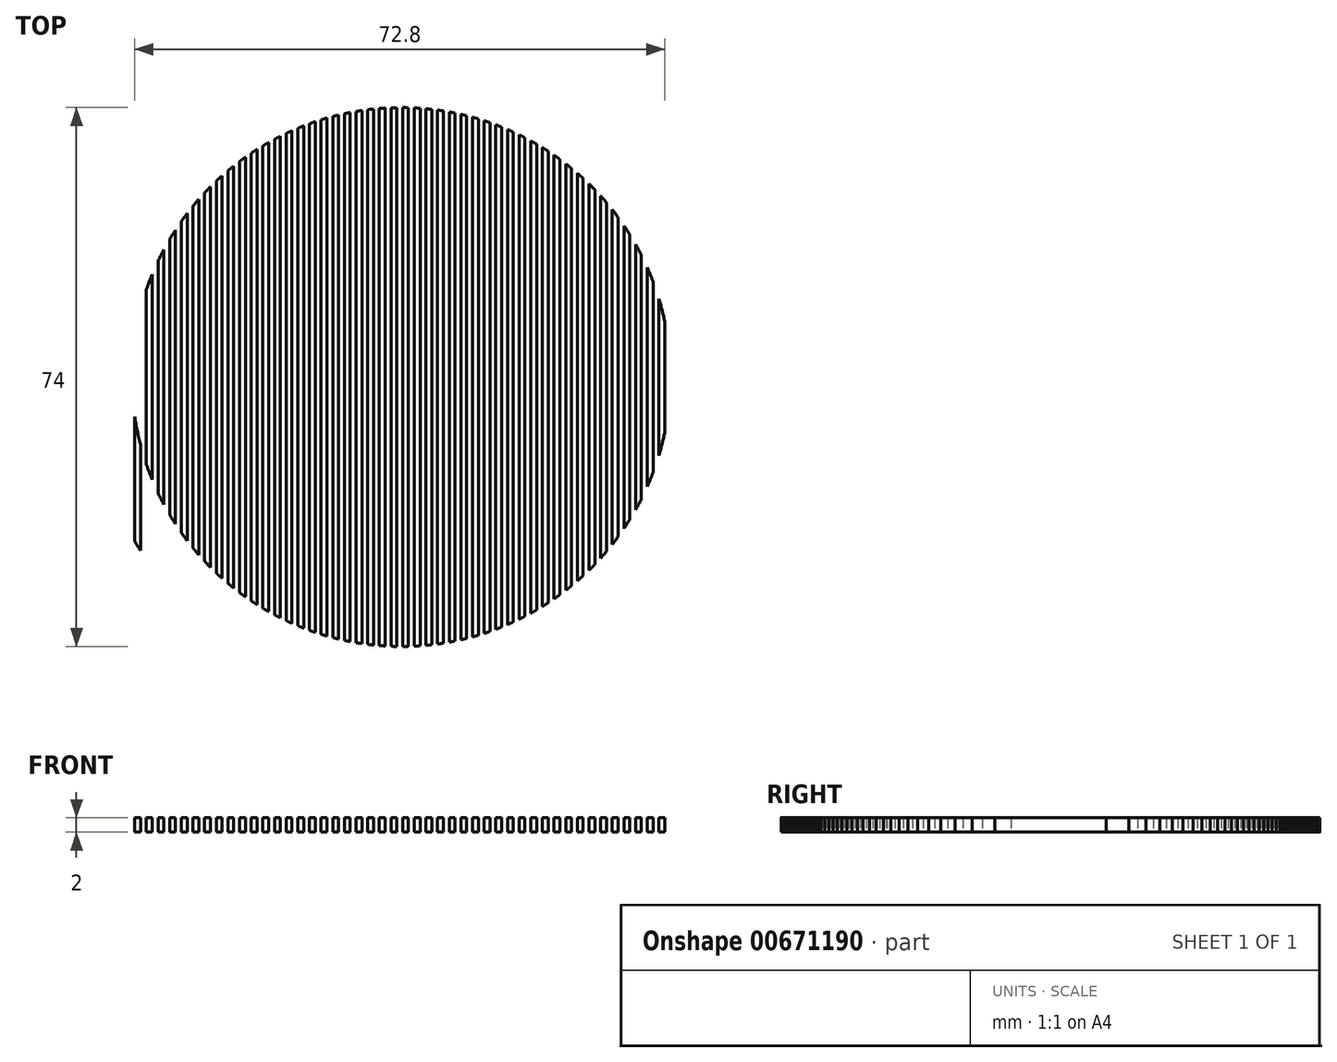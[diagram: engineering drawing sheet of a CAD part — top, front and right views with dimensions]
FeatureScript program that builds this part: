
annotation { "Feature Type Name" : "Feature", "Feature Type Description" : "" }
export const myFeature = defineFeature(function(context is Context, id is Id, definition is map)
    precondition{}
    {
        {
            var Q0;
            Q0=qCreatedBy(makeId("Top.planeOp"),FACE);
            var sketch = newSketch(context, id + "F0", { "sketchPlane" : qUnion([Q0])});
            skLineSegment(sketch, "E0.bottom", {"start": v(0, 0) * mm, "end": v(86, 0) * mm});
            skLineSegment(sketch, "E0.top", {"start": v(0, 86) * mm, "end": v(86, 86) * mm});
            skLineSegment(sketch, "E0.left", {"start": v(0, 0) * mm, "end": v(0, 86) * mm});
            skLineSegment(sketch, "E0.right", {"start": v(86, 0) * mm, "end": v(86, 86) * mm});
            skLineSegment(sketch, "E1.bottom", {"start": v(0, 86) * mm, "end": v(0.8, 86) * mm});
            skLineSegment(sketch, "E1.top", {"start": v(0, 0) * mm, "end": v(0.8, 0) * mm});
            skLineSegment(sketch, "E1.left", {"start": v(0, 86) * mm, "end": v(0, 0) * mm});
            skLineSegment(sketch, "E1.right", {"start": v(0.8, 86) * mm, "end": v(0.8, 0) * mm});
            skLineSegment(sketch, "E2.1.0.0", {"start": v(1.6, 86) * mm, "end": v(1.6, 0) * mm});
            skLineSegment(sketch, "E2.2.0.0", {"start": v(2.4, 86) * mm, "end": v(2.4, 0) * mm});
            skLineSegment(sketch, "E2.3.0.0", {"start": v(3.2, 86) * mm, "end": v(3.2, 0) * mm});
            skLineSegment(sketch, "E2.4.0.0", {"start": v(4, 86) * mm, "end": v(4, 0) * mm});
            skLineSegment(sketch, "E2.5.0.0", {"start": v(4.8, 86) * mm, "end": v(4.8, 0) * mm});
            skLineSegment(sketch, "E2.6.0.0", {"start": v(5.6, 86) * mm, "end": v(5.6, 0) * mm});
            skLineSegment(sketch, "E2.7.0.0", {"start": v(6.4, 86) * mm, "end": v(6.4, 0) * mm});
            skLineSegment(sketch, "E2.8.0.0", {"start": v(7.2, 86) * mm, "end": v(7.2, 0) * mm});
            skLineSegment(sketch, "E2.9.0.0", {"start": v(8, 86) * mm, "end": v(8, 0) * mm});
            skLineSegment(sketch, "E2.10.0.0", {"start": v(8.8, 86) * mm, "end": v(8.8, 0) * mm});
            skLineSegment(sketch, "E2.11.0.0", {"start": v(9.6, 86) * mm, "end": v(9.6, 0) * mm});
            skLineSegment(sketch, "E2.12.0.0", {"start": v(10.4, 86) * mm, "end": v(10.4, 0) * mm});
            skLineSegment(sketch, "E2.13.0.0", {"start": v(11.2, 86) * mm, "end": v(11.2, 0) * mm});
            skLineSegment(sketch, "E2.14.0.0", {"start": v(12, 86) * mm, "end": v(12, 0) * mm});
            skLineSegment(sketch, "E2.15.0.0", {"start": v(12.8, 86) * mm, "end": v(12.8, 0) * mm});
            skLineSegment(sketch, "E2.16.0.0", {"start": v(13.6, 86) * mm, "end": v(13.6, 0) * mm});
            skLineSegment(sketch, "E2.17.0.0", {"start": v(14.4, 86) * mm, "end": v(14.4, 0) * mm});
            skLineSegment(sketch, "E2.18.0.0", {"start": v(15.2, 86) * mm, "end": v(15.2, 0) * mm});
            skLineSegment(sketch, "E2.19.0.0", {"start": v(16, 86) * mm, "end": v(16, 0) * mm});
            skLineSegment(sketch, "E2.20.0.0", {"start": v(16.8, 86) * mm, "end": v(16.8, 0) * mm});
            skLineSegment(sketch, "E2.21.0.0", {"start": v(17.6, 86) * mm, "end": v(17.6, 0) * mm});
            skLineSegment(sketch, "E2.22.0.0", {"start": v(18.4, 86) * mm, "end": v(18.4, 0) * mm});
            skLineSegment(sketch, "E2.23.0.0", {"start": v(19.2, 86) * mm, "end": v(19.2, 0) * mm});
            skLineSegment(sketch, "E2.24.0.0", {"start": v(20, 86) * mm, "end": v(20, 0) * mm});
            skLineSegment(sketch, "E2.25.0.0", {"start": v(20.8, 86) * mm, "end": v(20.8, 0) * mm});
            skLineSegment(sketch, "E2.26.0.0", {"start": v(21.6, 86) * mm, "end": v(21.6, 0) * mm});
            skLineSegment(sketch, "E2.27.0.0", {"start": v(22.4, 86) * mm, "end": v(22.4, 0) * mm});
            skLineSegment(sketch, "E2.28.0.0", {"start": v(23.2, 86) * mm, "end": v(23.2, 0) * mm});
            skLineSegment(sketch, "E2.29.0.0", {"start": v(24, 86) * mm, "end": v(24, 0) * mm});
            skLineSegment(sketch, "E2.30.0.0", {"start": v(24.8, 86) * mm, "end": v(24.8, 0) * mm});
            skLineSegment(sketch, "E2.31.0.0", {"start": v(25.6, 86) * mm, "end": v(25.6, 0) * mm});
            skLineSegment(sketch, "E2.32.0.0", {"start": v(26.4, 86) * mm, "end": v(26.4, 0) * mm});
            skLineSegment(sketch, "E2.33.0.0", {"start": v(27.2, 86) * mm, "end": v(27.2, 0) * mm});
            skLineSegment(sketch, "E2.34.0.0", {"start": v(28, 86) * mm, "end": v(28, 0) * mm});
            skLineSegment(sketch, "E2.35.0.0", {"start": v(28.8, 86) * mm, "end": v(28.8, 0) * mm});
            skLineSegment(sketch, "E2.36.0.0", {"start": v(29.6, 86) * mm, "end": v(29.6, 0) * mm});
            skLineSegment(sketch, "E2.37.0.0", {"start": v(30.4, 86) * mm, "end": v(30.4, 0) * mm});
            skLineSegment(sketch, "E2.38.0.0", {"start": v(31.2, 86) * mm, "end": v(31.2, 0) * mm});
            skLineSegment(sketch, "E2.39.0.0", {"start": v(32, 86) * mm, "end": v(32, 0) * mm});
            skLineSegment(sketch, "E2.40.0.0", {"start": v(32.8, 86) * mm, "end": v(32.8, 0) * mm});
            skLineSegment(sketch, "E2.41.0.0", {"start": v(33.6, 86) * mm, "end": v(33.6, 0) * mm});
            skLineSegment(sketch, "E2.42.0.0", {"start": v(34.4, 86) * mm, "end": v(34.4, 0) * mm});
            skLineSegment(sketch, "E2.43.0.0", {"start": v(35.2, 86) * mm, "end": v(35.2, 0) * mm});
            skLineSegment(sketch, "E2.44.0.0", {"start": v(36, 86) * mm, "end": v(36, 0) * mm});
            skLineSegment(sketch, "E2.45.0.0", {"start": v(36.8, 86) * mm, "end": v(36.8, 0) * mm});
            skLineSegment(sketch, "E2.46.0.0", {"start": v(37.6, 86) * mm, "end": v(37.6, 0) * mm});
            skLineSegment(sketch, "E2.47.0.0", {"start": v(38.4, 86) * mm, "end": v(38.4, 0) * mm});
            skLineSegment(sketch, "E2.48.0.0", {"start": v(39.2, 86) * mm, "end": v(39.2, 0) * mm});
            skLineSegment(sketch, "E2.49.0.0", {"start": v(40, 86) * mm, "end": v(40, 0) * mm});
            skLineSegment(sketch, "E2.50.0.0", {"start": v(40.8, 86) * mm, "end": v(40.8, 0) * mm});
            skLineSegment(sketch, "E2.51.0.0", {"start": v(41.6, 86) * mm, "end": v(41.6, 0) * mm});
            skLineSegment(sketch, "E2.52.0.0", {"start": v(42.4, 86) * mm, "end": v(42.4, 0) * mm});
            skLineSegment(sketch, "E2.53.0.0", {"start": v(43.2, 86) * mm, "end": v(43.2, 0) * mm});
            skLineSegment(sketch, "E2.54.0.0", {"start": v(44, 86) * mm, "end": v(44, 0) * mm});
            skLineSegment(sketch, "E2.55.0.0", {"start": v(44.8, 86) * mm, "end": v(44.8, 0) * mm});
            skLineSegment(sketch, "E2.56.0.0", {"start": v(45.6, 86) * mm, "end": v(45.6, 0) * mm});
            skLineSegment(sketch, "E2.57.0.0", {"start": v(46.4, 86) * mm, "end": v(46.4, 0) * mm});
            skLineSegment(sketch, "E2.58.0.0", {"start": v(47.2, 86) * mm, "end": v(47.2, 0) * mm});
            skLineSegment(sketch, "E2.59.0.0", {"start": v(48, 86) * mm, "end": v(48, 0) * mm});
            skLineSegment(sketch, "E2.60.0.0", {"start": v(48.8, 86) * mm, "end": v(48.8, 0) * mm});
            skLineSegment(sketch, "E2.61.0.0", {"start": v(49.6, 86) * mm, "end": v(49.6, 0) * mm});
            skLineSegment(sketch, "E2.62.0.0", {"start": v(50.4, 86) * mm, "end": v(50.4, 0) * mm});
            skLineSegment(sketch, "E2.63.0.0", {"start": v(51.2, 86) * mm, "end": v(51.2, 0) * mm});
            skLineSegment(sketch, "E2.64.0.0", {"start": v(52, 86) * mm, "end": v(52, 0) * mm});
            skLineSegment(sketch, "E2.65.0.0", {"start": v(52.8, 86) * mm, "end": v(52.8, 0) * mm});
            skLineSegment(sketch, "E2.66.0.0", {"start": v(53.6, 86) * mm, "end": v(53.6, 0) * mm});
            skLineSegment(sketch, "E2.67.0.0", {"start": v(54.4, 86) * mm, "end": v(54.4, 0) * mm});
            skLineSegment(sketch, "E2.68.0.0", {"start": v(55.2, 86) * mm, "end": v(55.2, 0) * mm});
            skLineSegment(sketch, "E2.69.0.0", {"start": v(56, 86) * mm, "end": v(56, 0) * mm});
            skLineSegment(sketch, "E2.70.0.0", {"start": v(56.8, 86) * mm, "end": v(56.8, 0) * mm});
            skLineSegment(sketch, "E2.71.0.0", {"start": v(57.6, 86) * mm, "end": v(57.6, 0) * mm});
            skLineSegment(sketch, "E2.72.0.0", {"start": v(58.4, 86) * mm, "end": v(58.4, 0) * mm});
            skLineSegment(sketch, "E2.73.0.0", {"start": v(59.2, 86) * mm, "end": v(59.2, 0) * mm});
            skLineSegment(sketch, "E2.74.0.0", {"start": v(60, 86) * mm, "end": v(60, 0) * mm});
            skLineSegment(sketch, "E2.75.0.0", {"start": v(60.8, 86) * mm, "end": v(60.8, 0) * mm});
            skLineSegment(sketch, "E2.76.0.0", {"start": v(61.6, 86) * mm, "end": v(61.6, 0) * mm});
            skLineSegment(sketch, "E2.77.0.0", {"start": v(62.4, 86) * mm, "end": v(62.4, 0) * mm});
            skLineSegment(sketch, "E2.78.0.0", {"start": v(63.2, 86) * mm, "end": v(63.2, 0) * mm});
            skLineSegment(sketch, "E2.79.0.0", {"start": v(64, 86) * mm, "end": v(64, 0) * mm});
            skLineSegment(sketch, "E2.80.0.0", {"start": v(64.8, 86) * mm, "end": v(64.8, 0) * mm});
            skLineSegment(sketch, "E2.81.0.0", {"start": v(65.6, 86) * mm, "end": v(65.6, 0) * mm});
            skLineSegment(sketch, "E2.82.0.0", {"start": v(66.4, 86) * mm, "end": v(66.4, 0) * mm});
            skLineSegment(sketch, "E2.83.0.0", {"start": v(67.2, 86) * mm, "end": v(67.2, 0) * mm});
            skLineSegment(sketch, "E2.84.0.0", {"start": v(68, 86) * mm, "end": v(68, 0) * mm});
            skLineSegment(sketch, "E2.85.0.0", {"start": v(68.8, 86) * mm, "end": v(68.8, 0) * mm});
            skLineSegment(sketch, "E2.86.0.0", {"start": v(69.6, 86) * mm, "end": v(69.6, 0) * mm});
            skLineSegment(sketch, "E2.87.0.0", {"start": v(70.4, 86) * mm, "end": v(70.4, 0) * mm});
            skLineSegment(sketch, "E2.88.0.0", {"start": v(71.2, 86) * mm, "end": v(71.2, 0) * mm});
            skLineSegment(sketch, "E2.89.0.0", {"start": v(72, 86) * mm, "end": v(72, 0) * mm});
            skLineSegment(sketch, "E2.90.0.0", {"start": v(72.8, 86) * mm, "end": v(72.8, 0) * mm});
            skLineSegment(sketch, "E2.91.0.0", {"start": v(73.6, 86) * mm, "end": v(73.6, 0) * mm});
            skLineSegment(sketch, "E2.92.0.0", {"start": v(74.4, 86) * mm, "end": v(74.4, 0) * mm});
            skLineSegment(sketch, "E2.93.0.0", {"start": v(75.2, 86) * mm, "end": v(75.2, 0) * mm});
            skLineSegment(sketch, "E2.94.0.0", {"start": v(76, 86) * mm, "end": v(76, 0) * mm});
            skLineSegment(sketch, "E2.95.0.0", {"start": v(76.8, 86) * mm, "end": v(76.8, 0) * mm});
            skLineSegment(sketch, "E2.96.0.0", {"start": v(77.6, 86) * mm, "end": v(77.6, 0) * mm});
            skLineSegment(sketch, "E2.97.0.0", {"start": v(78.4, 86) * mm, "end": v(78.4, 0) * mm});
            skLineSegment(sketch, "E2.98.0.0", {"start": v(79.2, 86) * mm, "end": v(79.2, 0) * mm});
            skLineSegment(sketch, "E2.99.0.0", {"start": v(80, 86) * mm, "end": v(80, 0) * mm});
            skLineSegment(sketch, "E2.direction1", {"start": v(0.8, 0) * mm, "end": v(1.6, 0) * mm, "construction": true});
            skLineSegment(sketch, "E3", {"start": v(86, 86) * mm, "end": v(0, 0) * mm, "construction": true});
            skCircle(sketch, "E4", {"center": v(43, 43) * mm, "radius": 43 * mm});
            skCircle(sketch, "E5", {"center": v(43, 43) * mm, "radius": 37 * mm});
            skSolve(sketch);
        }
        {
            var Q0;
            {var subQ0=sQuery(id+"F0.wireOp",EDGE,"E5");var subQ1=sQuery(id+"F0.wireOp",EDGE,"E2.7.0.0");var subQ2=makeQuery(id+"F0.imprint","INTERSECT",VERTEX,{"disambiguationData":[OD(0.0)],"derivedFrom":[subQ1,subQ0]});Q0=makeQuery(id+"F0.imprint","IMPRINT",FACE,{"disambiguationData":[TD([[makeQuery(id+"F0.imprint","IMPRINT",EDGE,{"disambiguationData":[TD([[subQ2,-1.0]])],"derivedFrom":subQ1}),1.0]])]});}
            var Q1;
            {var subQ0=sQuery(id+"F0.wireOp",EDGE,"E5");var subQ1=sQuery(id+"F0.wireOp",EDGE,"E2.9.0.0");var subQ2=makeQuery(id+"F0.imprint","INTERSECT",VERTEX,{"disambiguationData":[OD(0.0)],"derivedFrom":[subQ1,subQ0]});Q1=makeQuery(id+"F0.imprint","IMPRINT",FACE,{"disambiguationData":[TD([[makeQuery(id+"F0.imprint","IMPRINT",EDGE,{"disambiguationData":[TD([[subQ2,-1.0]])],"derivedFrom":subQ1}),1.0]])]});}
            var Q2;
            {var subQ0=sQuery(id+"F0.wireOp",EDGE,"E5");var subQ1=sQuery(id+"F0.wireOp",EDGE,"E2.11.0.0");var subQ2=makeQuery(id+"F0.imprint","INTERSECT",VERTEX,{"disambiguationData":[OD(0.0)],"derivedFrom":[subQ1,subQ0]});Q2=makeQuery(id+"F0.imprint","IMPRINT",FACE,{"disambiguationData":[TD([[makeQuery(id+"F0.imprint","IMPRINT",EDGE,{"disambiguationData":[TD([[subQ2,-1.0]])],"derivedFrom":subQ1}),1.0]])]});}
            var Q3;
            {var subQ0=sQuery(id+"F0.wireOp",EDGE,"E5");var subQ1=sQuery(id+"F0.wireOp",EDGE,"E2.13.0.0");var subQ2=makeQuery(id+"F0.imprint","INTERSECT",VERTEX,{"disambiguationData":[OD(0.0)],"derivedFrom":[subQ1,subQ0]});Q3=makeQuery(id+"F0.imprint","IMPRINT",FACE,{"disambiguationData":[TD([[makeQuery(id+"F0.imprint","IMPRINT",EDGE,{"disambiguationData":[TD([[subQ2,-1.0]])],"derivedFrom":subQ1}),1.0]])]});}
            var Q4;
            {var subQ0=sQuery(id+"F0.wireOp",EDGE,"E5");var subQ1=sQuery(id+"F0.wireOp",EDGE,"E2.15.0.0");var subQ2=makeQuery(id+"F0.imprint","INTERSECT",VERTEX,{"disambiguationData":[OD(0.0)],"derivedFrom":[subQ1,subQ0]});Q4=makeQuery(id+"F0.imprint","IMPRINT",FACE,{"disambiguationData":[TD([[makeQuery(id+"F0.imprint","IMPRINT",EDGE,{"disambiguationData":[TD([[subQ2,-1.0]])],"derivedFrom":subQ1}),1.0]])]});}
            var Q5;
            {var subQ0=sQuery(id+"F0.wireOp",EDGE,"E5");var subQ1=sQuery(id+"F0.wireOp",EDGE,"E2.17.0.0");var subQ2=makeQuery(id+"F0.imprint","INTERSECT",VERTEX,{"disambiguationData":[OD(0.0)],"derivedFrom":[subQ1,subQ0]});Q5=makeQuery(id+"F0.imprint","IMPRINT",FACE,{"disambiguationData":[TD([[makeQuery(id+"F0.imprint","IMPRINT",EDGE,{"disambiguationData":[TD([[subQ2,-1.0]])],"derivedFrom":subQ1}),1.0]])]});}
            var Q6;
            {var subQ0=sQuery(id+"F0.wireOp",EDGE,"E5");var subQ1=sQuery(id+"F0.wireOp",EDGE,"E2.19.0.0");var subQ2=makeQuery(id+"F0.imprint","INTERSECT",VERTEX,{"disambiguationData":[OD(0.0)],"derivedFrom":[subQ1,subQ0]});Q6=makeQuery(id+"F0.imprint","IMPRINT",FACE,{"disambiguationData":[TD([[makeQuery(id+"F0.imprint","IMPRINT",EDGE,{"disambiguationData":[TD([[subQ2,-1.0]])],"derivedFrom":subQ1}),1.0]])]});}
            var Q7;
            {var subQ0=sQuery(id+"F0.wireOp",EDGE,"E5");var subQ1=sQuery(id+"F0.wireOp",EDGE,"E2.21.0.0");var subQ2=makeQuery(id+"F0.imprint","INTERSECT",VERTEX,{"disambiguationData":[OD(0.0)],"derivedFrom":[subQ1,subQ0]});Q7=makeQuery(id+"F0.imprint","IMPRINT",FACE,{"disambiguationData":[TD([[makeQuery(id+"F0.imprint","IMPRINT",EDGE,{"disambiguationData":[TD([[subQ2,-1.0]])],"derivedFrom":subQ1}),1.0]])]});}
            var Q8;
            {var subQ0=sQuery(id+"F0.wireOp",EDGE,"E5");var subQ1=sQuery(id+"F0.wireOp",EDGE,"E2.23.0.0");var subQ2=makeQuery(id+"F0.imprint","INTERSECT",VERTEX,{"disambiguationData":[OD(0.0)],"derivedFrom":[subQ1,subQ0]});Q8=makeQuery(id+"F0.imprint","IMPRINT",FACE,{"disambiguationData":[TD([[makeQuery(id+"F0.imprint","IMPRINT",EDGE,{"disambiguationData":[TD([[subQ2,-1.0]])],"derivedFrom":subQ1}),1.0]])]});}
            var Q9;
            {var subQ0=sQuery(id+"F0.wireOp",EDGE,"E5");var subQ1=sQuery(id+"F0.wireOp",EDGE,"E2.25.0.0");var subQ2=makeQuery(id+"F0.imprint","INTERSECT",VERTEX,{"disambiguationData":[OD(0.0)],"derivedFrom":[subQ1,subQ0]});Q9=makeQuery(id+"F0.imprint","IMPRINT",FACE,{"disambiguationData":[TD([[makeQuery(id+"F0.imprint","IMPRINT",EDGE,{"disambiguationData":[TD([[subQ2,-1.0]])],"derivedFrom":subQ1}),1.0]])]});}
            var Q10;
            {var subQ0=sQuery(id+"F0.wireOp",EDGE,"E5");var subQ1=sQuery(id+"F0.wireOp",EDGE,"E2.27.0.0");var subQ2=makeQuery(id+"F0.imprint","INTERSECT",VERTEX,{"disambiguationData":[OD(0.0)],"derivedFrom":[subQ1,subQ0]});Q10=makeQuery(id+"F0.imprint","IMPRINT",FACE,{"disambiguationData":[TD([[makeQuery(id+"F0.imprint","IMPRINT",EDGE,{"disambiguationData":[TD([[subQ2,-1.0]])],"derivedFrom":subQ1}),1.0]])]});}
            var Q11;
            {var subQ0=sQuery(id+"F0.wireOp",EDGE,"E5");var subQ1=sQuery(id+"F0.wireOp",EDGE,"E2.29.0.0");var subQ2=makeQuery(id+"F0.imprint","INTERSECT",VERTEX,{"disambiguationData":[OD(0.0)],"derivedFrom":[subQ1,subQ0]});Q11=makeQuery(id+"F0.imprint","IMPRINT",FACE,{"disambiguationData":[TD([[makeQuery(id+"F0.imprint","IMPRINT",EDGE,{"disambiguationData":[TD([[subQ2,-1.0]])],"derivedFrom":subQ1}),1.0]])]});}
            var Q12;
            {var subQ0=sQuery(id+"F0.wireOp",EDGE,"E5");var subQ1=sQuery(id+"F0.wireOp",EDGE,"E2.31.0.0");var subQ2=makeQuery(id+"F0.imprint","INTERSECT",VERTEX,{"disambiguationData":[OD(0.0)],"derivedFrom":[subQ1,subQ0]});Q12=makeQuery(id+"F0.imprint","IMPRINT",FACE,{"disambiguationData":[TD([[makeQuery(id+"F0.imprint","IMPRINT",EDGE,{"disambiguationData":[TD([[subQ2,-1.0]])],"derivedFrom":subQ1}),1.0]])]});}
            var Q13;
            {var subQ0=sQuery(id+"F0.wireOp",EDGE,"E5");var subQ1=sQuery(id+"F0.wireOp",EDGE,"E2.33.0.0");var subQ2=makeQuery(id+"F0.imprint","INTERSECT",VERTEX,{"disambiguationData":[OD(0.0)],"derivedFrom":[subQ1,subQ0]});Q13=makeQuery(id+"F0.imprint","IMPRINT",FACE,{"disambiguationData":[TD([[makeQuery(id+"F0.imprint","IMPRINT",EDGE,{"disambiguationData":[TD([[subQ2,-1.0]])],"derivedFrom":subQ1}),1.0]])]});}
            var Q14;
            {var subQ0=sQuery(id+"F0.wireOp",EDGE,"E5");var subQ1=sQuery(id+"F0.wireOp",EDGE,"E2.35.0.0");var subQ2=makeQuery(id+"F0.imprint","INTERSECT",VERTEX,{"disambiguationData":[OD(0.0)],"derivedFrom":[subQ1,subQ0]});Q14=makeQuery(id+"F0.imprint","IMPRINT",FACE,{"disambiguationData":[TD([[makeQuery(id+"F0.imprint","IMPRINT",EDGE,{"disambiguationData":[TD([[subQ2,-1.0]])],"derivedFrom":subQ1}),1.0]])]});}
            var Q15;
            {var subQ0=sQuery(id+"F0.wireOp",EDGE,"E5");var subQ1=sQuery(id+"F0.wireOp",EDGE,"E2.37.0.0");var subQ2=makeQuery(id+"F0.imprint","INTERSECT",VERTEX,{"disambiguationData":[OD(0.0)],"derivedFrom":[subQ1,subQ0]});Q15=makeQuery(id+"F0.imprint","IMPRINT",FACE,{"disambiguationData":[TD([[makeQuery(id+"F0.imprint","IMPRINT",EDGE,{"disambiguationData":[TD([[subQ2,-1.0]])],"derivedFrom":subQ1}),1.0]])]});}
            var Q16;
            {var subQ0=sQuery(id+"F0.wireOp",EDGE,"E5");var subQ1=sQuery(id+"F0.wireOp",EDGE,"E2.39.0.0");var subQ2=makeQuery(id+"F0.imprint","INTERSECT",VERTEX,{"disambiguationData":[OD(0.0)],"derivedFrom":[subQ1,subQ0]});Q16=makeQuery(id+"F0.imprint","IMPRINT",FACE,{"disambiguationData":[TD([[makeQuery(id+"F0.imprint","IMPRINT",EDGE,{"disambiguationData":[TD([[subQ2,-1.0]])],"derivedFrom":subQ1}),1.0]])]});}
            var Q17;
            {var subQ0=sQuery(id+"F0.wireOp",EDGE,"E5");var subQ1=sQuery(id+"F0.wireOp",EDGE,"E2.41.0.0");var subQ2=makeQuery(id+"F0.imprint","INTERSECT",VERTEX,{"disambiguationData":[OD(0.0)],"derivedFrom":[subQ1,subQ0]});Q17=makeQuery(id+"F0.imprint","IMPRINT",FACE,{"disambiguationData":[TD([[makeQuery(id+"F0.imprint","IMPRINT",EDGE,{"disambiguationData":[TD([[subQ2,-1.0]])],"derivedFrom":subQ1}),1.0]])]});}
            var Q18;
            {var subQ0=sQuery(id+"F0.wireOp",EDGE,"E5");var subQ1=sQuery(id+"F0.wireOp",EDGE,"E2.43.0.0");var subQ2=makeQuery(id+"F0.imprint","INTERSECT",VERTEX,{"disambiguationData":[OD(0.0)],"derivedFrom":[subQ1,subQ0]});Q18=makeQuery(id+"F0.imprint","IMPRINT",FACE,{"disambiguationData":[TD([[makeQuery(id+"F0.imprint","IMPRINT",EDGE,{"disambiguationData":[TD([[subQ2,-1.0]])],"derivedFrom":subQ1}),1.0]])]});}
            var Q19;
            {var subQ0=sQuery(id+"F0.wireOp",EDGE,"E5");var subQ1=sQuery(id+"F0.wireOp",EDGE,"E2.45.0.0");var subQ2=makeQuery(id+"F0.imprint","INTERSECT",VERTEX,{"disambiguationData":[OD(0.0)],"derivedFrom":[subQ1,subQ0]});Q19=makeQuery(id+"F0.imprint","IMPRINT",FACE,{"disambiguationData":[TD([[makeQuery(id+"F0.imprint","IMPRINT",EDGE,{"disambiguationData":[TD([[subQ2,-1.0]])],"derivedFrom":subQ1}),1.0]])]});}
            var Q20;
            {var subQ0=sQuery(id+"F0.wireOp",EDGE,"E5");var subQ1=sQuery(id+"F0.wireOp",EDGE,"E2.47.0.0");var subQ2=makeQuery(id+"F0.imprint","INTERSECT",VERTEX,{"disambiguationData":[OD(0.0)],"derivedFrom":[subQ1,subQ0]});Q20=makeQuery(id+"F0.imprint","IMPRINT",FACE,{"disambiguationData":[TD([[makeQuery(id+"F0.imprint","IMPRINT",EDGE,{"disambiguationData":[TD([[subQ2,-1.0]])],"derivedFrom":subQ1}),1.0]])]});}
            var Q21;
            {var subQ0=sQuery(id+"F0.wireOp",EDGE,"E5");var subQ1=sQuery(id+"F0.wireOp",EDGE,"E2.49.0.0");var subQ2=makeQuery(id+"F0.imprint","INTERSECT",VERTEX,{"disambiguationData":[OD(0.0)],"derivedFrom":[subQ1,subQ0]});Q21=makeQuery(id+"F0.imprint","IMPRINT",FACE,{"disambiguationData":[TD([[makeQuery(id+"F0.imprint","IMPRINT",EDGE,{"disambiguationData":[TD([[subQ2,-1.0]])],"derivedFrom":subQ1}),1.0]])]});}
            var Q22;
            {var subQ0=sQuery(id+"F0.wireOp",EDGE,"E5");var subQ1=sQuery(id+"F0.wireOp",EDGE,"E2.51.0.0");var subQ2=makeQuery(id+"F0.imprint","INTERSECT",VERTEX,{"disambiguationData":[OD(0.0)],"derivedFrom":[subQ1,subQ0]});Q22=makeQuery(id+"F0.imprint","IMPRINT",FACE,{"disambiguationData":[TD([[makeQuery(id+"F0.imprint","IMPRINT",EDGE,{"disambiguationData":[TD([[subQ2,-1.0]])],"derivedFrom":subQ1}),1.0]])]});}
            var Q23;
            {var subQ0=sQuery(id+"F0.wireOp",EDGE,"E5");var subQ1=sQuery(id+"F0.wireOp",EDGE,"E2.53.0.0");var subQ2=makeQuery(id+"F0.imprint","INTERSECT",VERTEX,{"disambiguationData":[OD(0.0)],"derivedFrom":[subQ1,subQ0]});Q23=makeQuery(id+"F0.imprint","IMPRINT",FACE,{"disambiguationData":[TD([[makeQuery(id+"F0.imprint","IMPRINT",EDGE,{"disambiguationData":[TD([[subQ2,-1.0]])],"derivedFrom":subQ1}),1.0]])]});}
            var Q24;
            {var subQ0=sQuery(id+"F0.wireOp",EDGE,"E5");var subQ1=sQuery(id+"F0.wireOp",EDGE,"E2.55.0.0");var subQ2=makeQuery(id+"F0.imprint","INTERSECT",VERTEX,{"disambiguationData":[OD(0.0)],"derivedFrom":[subQ1,subQ0]});Q24=makeQuery(id+"F0.imprint","IMPRINT",FACE,{"disambiguationData":[TD([[makeQuery(id+"F0.imprint","IMPRINT",EDGE,{"disambiguationData":[TD([[subQ2,-1.0]])],"derivedFrom":subQ1}),1.0]])]});}
            var Q25;
            {var subQ0=sQuery(id+"F0.wireOp",EDGE,"E5");var subQ1=sQuery(id+"F0.wireOp",EDGE,"E2.57.0.0");var subQ2=makeQuery(id+"F0.imprint","INTERSECT",VERTEX,{"disambiguationData":[OD(0.0)],"derivedFrom":[subQ1,subQ0]});Q25=makeQuery(id+"F0.imprint","IMPRINT",FACE,{"disambiguationData":[TD([[makeQuery(id+"F0.imprint","IMPRINT",EDGE,{"disambiguationData":[TD([[subQ2,-1.0]])],"derivedFrom":subQ1}),1.0]])]});}
            var Q26;
            {var subQ0=sQuery(id+"F0.wireOp",EDGE,"E5");var subQ1=sQuery(id+"F0.wireOp",EDGE,"E2.59.0.0");var subQ2=makeQuery(id+"F0.imprint","INTERSECT",VERTEX,{"disambiguationData":[OD(0.0)],"derivedFrom":[subQ1,subQ0]});Q26=makeQuery(id+"F0.imprint","IMPRINT",FACE,{"disambiguationData":[TD([[makeQuery(id+"F0.imprint","IMPRINT",EDGE,{"disambiguationData":[TD([[subQ2,-1.0]])],"derivedFrom":subQ1}),1.0]])]});}
            var Q27;
            {var subQ0=sQuery(id+"F0.wireOp",EDGE,"E5");var subQ1=sQuery(id+"F0.wireOp",EDGE,"E2.61.0.0");var subQ2=makeQuery(id+"F0.imprint","INTERSECT",VERTEX,{"disambiguationData":[OD(0.0)],"derivedFrom":[subQ1,subQ0]});Q27=makeQuery(id+"F0.imprint","IMPRINT",FACE,{"disambiguationData":[TD([[makeQuery(id+"F0.imprint","IMPRINT",EDGE,{"disambiguationData":[TD([[subQ2,-1.0]])],"derivedFrom":subQ1}),1.0]])]});}
            var Q28;
            {var subQ0=sQuery(id+"F0.wireOp",EDGE,"E5");var subQ1=sQuery(id+"F0.wireOp",EDGE,"E2.63.0.0");var subQ2=makeQuery(id+"F0.imprint","INTERSECT",VERTEX,{"disambiguationData":[OD(0.0)],"derivedFrom":[subQ1,subQ0]});Q28=makeQuery(id+"F0.imprint","IMPRINT",FACE,{"disambiguationData":[TD([[makeQuery(id+"F0.imprint","IMPRINT",EDGE,{"disambiguationData":[TD([[subQ2,-1.0]])],"derivedFrom":subQ1}),1.0]])]});}
            var Q29;
            {var subQ0=sQuery(id+"F0.wireOp",EDGE,"E5");var subQ1=sQuery(id+"F0.wireOp",EDGE,"E2.65.0.0");var subQ2=makeQuery(id+"F0.imprint","INTERSECT",VERTEX,{"disambiguationData":[OD(0.0)],"derivedFrom":[subQ1,subQ0]});Q29=makeQuery(id+"F0.imprint","IMPRINT",FACE,{"disambiguationData":[TD([[makeQuery(id+"F0.imprint","IMPRINT",EDGE,{"disambiguationData":[TD([[subQ2,-1.0]])],"derivedFrom":subQ1}),1.0]])]});}
            var Q30;
            {var subQ0=sQuery(id+"F0.wireOp",EDGE,"E5");var subQ1=sQuery(id+"F0.wireOp",EDGE,"E2.67.0.0");var subQ2=makeQuery(id+"F0.imprint","INTERSECT",VERTEX,{"disambiguationData":[OD(0.0)],"derivedFrom":[subQ1,subQ0]});Q30=makeQuery(id+"F0.imprint","IMPRINT",FACE,{"disambiguationData":[TD([[makeQuery(id+"F0.imprint","IMPRINT",EDGE,{"disambiguationData":[TD([[subQ2,-1.0]])],"derivedFrom":subQ1}),1.0]])]});}
            var Q31;
            {var subQ0=sQuery(id+"F0.wireOp",EDGE,"E5");var subQ1=sQuery(id+"F0.wireOp",EDGE,"E2.71.0.0");var subQ2=makeQuery(id+"F0.imprint","INTERSECT",VERTEX,{"disambiguationData":[OD(0.0)],"derivedFrom":[subQ1,subQ0]});Q31=makeQuery(id+"F0.imprint","IMPRINT",FACE,{"disambiguationData":[TD([[makeQuery(id+"F0.imprint","IMPRINT",EDGE,{"disambiguationData":[TD([[subQ2,-1.0]])],"derivedFrom":subQ1}),1.0]])]});}
            var Q32;
            {var subQ0=sQuery(id+"F0.wireOp",EDGE,"E5");var subQ1=sQuery(id+"F0.wireOp",EDGE,"E2.69.0.0");var subQ2=makeQuery(id+"F0.imprint","INTERSECT",VERTEX,{"disambiguationData":[OD(0.0)],"derivedFrom":[subQ1,subQ0]});Q32=makeQuery(id+"F0.imprint","IMPRINT",FACE,{"disambiguationData":[TD([[makeQuery(id+"F0.imprint","IMPRINT",EDGE,{"disambiguationData":[TD([[subQ2,-1.0]])],"derivedFrom":subQ1}),1.0]])]});}
            var Q33;
            {var subQ0=sQuery(id+"F0.wireOp",EDGE,"E5");var subQ1=sQuery(id+"F0.wireOp",EDGE,"E2.73.0.0");var subQ2=makeQuery(id+"F0.imprint","INTERSECT",VERTEX,{"disambiguationData":[OD(0.0)],"derivedFrom":[subQ1,subQ0]});Q33=makeQuery(id+"F0.imprint","IMPRINT",FACE,{"disambiguationData":[TD([[makeQuery(id+"F0.imprint","IMPRINT",EDGE,{"disambiguationData":[TD([[subQ2,-1.0]])],"derivedFrom":subQ1}),1.0]])]});}
            var Q34;
            {var subQ0=sQuery(id+"F0.wireOp",EDGE,"E5");var subQ1=sQuery(id+"F0.wireOp",EDGE,"E2.75.0.0");var subQ2=makeQuery(id+"F0.imprint","INTERSECT",VERTEX,{"disambiguationData":[OD(0.0)],"derivedFrom":[subQ1,subQ0]});Q34=makeQuery(id+"F0.imprint","IMPRINT",FACE,{"disambiguationData":[TD([[makeQuery(id+"F0.imprint","IMPRINT",EDGE,{"disambiguationData":[TD([[subQ2,-1.0]])],"derivedFrom":subQ1}),1.0]])]});}
            var Q35;
            {var subQ0=sQuery(id+"F0.wireOp",EDGE,"E5");var subQ1=sQuery(id+"F0.wireOp",EDGE,"E2.77.0.0");var subQ2=makeQuery(id+"F0.imprint","INTERSECT",VERTEX,{"disambiguationData":[OD(0.0)],"derivedFrom":[subQ1,subQ0]});Q35=makeQuery(id+"F0.imprint","IMPRINT",FACE,{"disambiguationData":[TD([[makeQuery(id+"F0.imprint","IMPRINT",EDGE,{"disambiguationData":[TD([[subQ2,-1.0]])],"derivedFrom":subQ1}),1.0]])]});}
            var Q36;
            {var subQ0=sQuery(id+"F0.wireOp",EDGE,"E5");var subQ1=sQuery(id+"F0.wireOp",EDGE,"E2.79.0.0");var subQ2=makeQuery(id+"F0.imprint","INTERSECT",VERTEX,{"disambiguationData":[OD(0.0)],"derivedFrom":[subQ1,subQ0]});Q36=makeQuery(id+"F0.imprint","IMPRINT",FACE,{"disambiguationData":[TD([[makeQuery(id+"F0.imprint","IMPRINT",EDGE,{"disambiguationData":[TD([[subQ2,-1.0]])],"derivedFrom":subQ1}),1.0]])]});}
            var Q37;
            {var subQ0=sQuery(id+"F0.wireOp",EDGE,"E5");var subQ1=sQuery(id+"F0.wireOp",EDGE,"E2.81.0.0");var subQ2=makeQuery(id+"F0.imprint","INTERSECT",VERTEX,{"disambiguationData":[OD(0.0)],"derivedFrom":[subQ1,subQ0]});Q37=makeQuery(id+"F0.imprint","IMPRINT",FACE,{"disambiguationData":[TD([[makeQuery(id+"F0.imprint","IMPRINT",EDGE,{"disambiguationData":[TD([[subQ2,-1.0]])],"derivedFrom":subQ1}),1.0]])]});}
            var Q38;
            {var subQ0=sQuery(id+"F0.wireOp",EDGE,"E5");var subQ1=sQuery(id+"F0.wireOp",EDGE,"E2.83.0.0");var subQ2=makeQuery(id+"F0.imprint","INTERSECT",VERTEX,{"disambiguationData":[OD(0.0)],"derivedFrom":[subQ1,subQ0]});Q38=makeQuery(id+"F0.imprint","IMPRINT",FACE,{"disambiguationData":[TD([[makeQuery(id+"F0.imprint","IMPRINT",EDGE,{"disambiguationData":[TD([[subQ2,-1.0]])],"derivedFrom":subQ1}),1.0]])]});}
            var Q39;
            {var subQ0=sQuery(id+"F0.wireOp",EDGE,"E5");var subQ1=sQuery(id+"F0.wireOp",EDGE,"E2.85.0.0");var subQ2=makeQuery(id+"F0.imprint","INTERSECT",VERTEX,{"disambiguationData":[OD(0.0)],"derivedFrom":[subQ1,subQ0]});Q39=makeQuery(id+"F0.imprint","IMPRINT",FACE,{"disambiguationData":[TD([[makeQuery(id+"F0.imprint","IMPRINT",EDGE,{"disambiguationData":[TD([[subQ2,-1.0]])],"derivedFrom":subQ1}),1.0]])]});}
            var Q40;
            {var subQ0=sQuery(id+"F0.wireOp",EDGE,"E5");var subQ1=sQuery(id+"F0.wireOp",EDGE,"E2.87.0.0");var subQ2=makeQuery(id+"F0.imprint","INTERSECT",VERTEX,{"disambiguationData":[OD(0.0)],"derivedFrom":[subQ1,subQ0]});Q40=makeQuery(id+"F0.imprint","IMPRINT",FACE,{"disambiguationData":[TD([[makeQuery(id+"F0.imprint","IMPRINT",EDGE,{"disambiguationData":[TD([[subQ2,-1.0]])],"derivedFrom":subQ1}),1.0]])]});}
            var Q41;
            {var subQ0=sQuery(id+"F0.wireOp",EDGE,"E5");var subQ1=sQuery(id+"F0.wireOp",EDGE,"E2.89.0.0");var subQ2=makeQuery(id+"F0.imprint","INTERSECT",VERTEX,{"disambiguationData":[OD(0.0)],"derivedFrom":[subQ1,subQ0]});Q41=makeQuery(id+"F0.imprint","IMPRINT",FACE,{"disambiguationData":[TD([[makeQuery(id+"F0.imprint","IMPRINT",EDGE,{"disambiguationData":[TD([[subQ2,-1.0]])],"derivedFrom":subQ1}),1.0]])]});}
            var Q42;
            {var subQ0=sQuery(id+"F0.wireOp",EDGE,"E5");var subQ1=sQuery(id+"F0.wireOp",EDGE,"E2.91.0.0");var subQ2=makeQuery(id+"F0.imprint","INTERSECT",VERTEX,{"disambiguationData":[OD(0.0)],"derivedFrom":[subQ1,subQ0]});Q42=makeQuery(id+"F0.imprint","IMPRINT",FACE,{"disambiguationData":[TD([[makeQuery(id+"F0.imprint","IMPRINT",EDGE,{"disambiguationData":[TD([[subQ2,-1.0]])],"derivedFrom":subQ1}),1.0]])]});}
            var Q43;
            {var subQ0=sQuery(id+"F0.wireOp",EDGE,"E5");var subQ1=sQuery(id+"F0.wireOp",EDGE,"E2.93.0.0");var subQ2=makeQuery(id+"F0.imprint","INTERSECT",VERTEX,{"disambiguationData":[OD(0.0)],"derivedFrom":[subQ1,subQ0]});Q43=makeQuery(id+"F0.imprint","IMPRINT",FACE,{"disambiguationData":[TD([[makeQuery(id+"F0.imprint","IMPRINT",EDGE,{"disambiguationData":[TD([[subQ2,-1.0]])],"derivedFrom":subQ1}),1.0]])]});}
            var Q44;
            {var subQ0=sQuery(id+"F0.wireOp",EDGE,"E5");var subQ1=sQuery(id+"F0.wireOp",EDGE,"E2.95.0.0");var subQ2=makeQuery(id+"F0.imprint","INTERSECT",VERTEX,{"disambiguationData":[OD(0.0)],"derivedFrom":[subQ1,subQ0]});Q44=makeQuery(id+"F0.imprint","IMPRINT",FACE,{"disambiguationData":[TD([[makeQuery(id+"F0.imprint","IMPRINT",EDGE,{"disambiguationData":[TD([[subQ2,-1.0]])],"derivedFrom":subQ1}),1.0]])]});}
            var Q45;
            {var subQ0=sQuery(id+"F0.wireOp",EDGE,"E5");var subQ1=sQuery(id+"F0.wireOp",EDGE,"E2.97.0.0");var subQ2=makeQuery(id+"F0.imprint","INTERSECT",VERTEX,{"disambiguationData":[OD(0.0)],"derivedFrom":[subQ1,subQ0]});Q45=makeQuery(id+"F0.imprint","IMPRINT",FACE,{"disambiguationData":[TD([[makeQuery(id+"F0.imprint","IMPRINT",EDGE,{"disambiguationData":[TD([[subQ2,-1.0]])],"derivedFrom":subQ1}),1.0]])]});}
            extrude(context, id + "F1", {"entities" : qUnion([Q0, Q1, Q2, Q3, Q4, Q5, Q6, Q7, Q8, Q9, Q10, Q11, Q12, Q13, Q14, Q15, Q16, Q17, Q18, Q19, Q20, Q21, Q22, Q23, Q24, Q25, Q26, Q27, Q28, Q29, Q30, Q31, Q32, Q33, Q34, Q35, Q36, Q37, Q38, Q39, Q40, Q41, Q42, Q43, Q44, Q45]), "depth" : 2 * mm, "offsetDistance" : 25 * mm});
        }
    });
